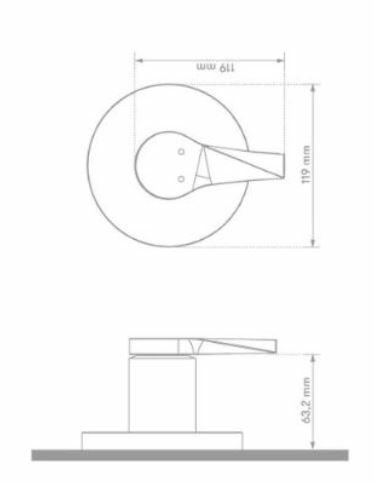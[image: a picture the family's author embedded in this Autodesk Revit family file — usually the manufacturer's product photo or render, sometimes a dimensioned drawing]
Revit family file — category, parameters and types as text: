
# Revit family: 01-3701-11SR MONOMANDO DUCHA VOGA
name_source: partatom
category: Aparatos sanitarios
revit_build: Autodesk Revit 2018 (Build: 20170223_1515(x64)
units: mm (PartAtom-declared; Revit-internal decimal feet)

## family parameters
Anfitrión = Cara
Compartido = No
Corte con vacíos al cargar = No
Cota de conector redondo = Diámetro de uso
Número OmniClass = 23.31.11.00
Punto de cálculo de habitación = No
Tipo de pieza = Normal

## types (1)
- 01-3701-11SR
    Alto base = 181 mm  [stored 0.593832 ft]
    Alto manija = 119.5 mm  [stored 0.39206 ft]
    Ancho base = 181 mm  [stored 0.593832 ft]
    Ancho manija = 44.5 mm
    Conexión AC = Sí
    Conexión AF = Sí
    Conexión de residuos = No
    Conexión de ventilación = No
    Descripción = Monomando ducha
    Elevación por defecto = 0 mm  [stored 0 ft]
    Fabricante = Gricol
    Imagen de tipo = MONOMANDO DUCHA VOGA.PNG
    Metal Laton Cromado = Metal Laton Cromado
    Metal Zamak Cromado = Metal Zamak Cromado
    Modelo = 01-3701-11SR
    Product Name = MONOMANDO DUCHA VOGA
    Profundidad manija = 73.5 mm
    URL = https://www.gricol.com

note: [stored X ft] marks values corroborated as IEEE doubles in the binary element streams (Revit-internal decimal feet)

## geometry (parser evidence)
native form markers: Blend x2, Sweep x6
no freeform markers — native parametric forms only
